# Revit family: M_Bifold-4 Panel
name_source: partatom
category: Doors
revit_build: Autodesk Revit Architecture 2014 (Build: 20130308_1515(x64)
units: mm (PartAtom-declared; Revit-internal decimal feet)

## types (4) — shared parameters
Analytic Construction = Metal
Construction Type Id = MDOOR
Door Material = Door - Panel
Frame Material = Door - Frame
Function = Interior
Heat Transfer Coefficient (U) = 3.7021 W/(m²·K)
Thermal Resistance (R) = 0.2701 (m²·K)/W
Thickness = 44 mm  [stored 0.144357 ft]
Trim Width = 76 mm  [stored 0.249344 ft]
Wall Closure = By host
zero-valued in all types: Solar Heat Gain Coefficient, Visual Light Transmittance

## per-type parameters (varying)
| type | Height | Width |
| 1220 x 2134mm | 2134 mm  [stored 7.00131 ft] | 1220 mm  [stored 4.00262 ft] |
| 1525 x 2134mm | 2134 mm  [stored 7.00131 ft] | 1525 mm  [stored 5.00328 ft] |
| 1830 x 2134mm | 2134 mm  [stored 7.00131 ft] | 1830 mm  [stored 6.00394 ft] |
| 1830 x 2032mm | 2032 mm | 1830 mm  [stored 6.00394 ft] |

note: [stored X ft] marks values corroborated as IEEE doubles in the binary element streams (Revit-internal decimal feet)

## geometry (parser evidence)
native form markers: Sweep x1
no freeform markers — native parametric forms only
